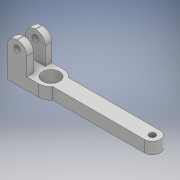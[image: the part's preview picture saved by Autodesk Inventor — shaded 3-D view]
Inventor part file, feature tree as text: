
AUTODESK INVENTOR PART (.ipt)
format: ipt  version: 2017 (Build 210142000, 142)  size: 168,960 bytes
history: native  units: mm
features: extrude x5, sketch x5, fillet x1
ambient origin geometry x8: Origin, YZ Plane, XZ Plane, XY Plane, X Axis, Y Axis, Z Axis, Center Point
bodies: Solid1 (feature_tree)
feature tree (11):
  extrude  "Extrusion1"  Depth=5.0mm
  extrude  "Extrusion2"  Depth=15.0mm TaperAngle=0.0deg
  extrude  "Extrusion3"  Depth=15.0mm
  fillet  "Fillet1"  Radius=35.0mm
  extrude  "Extrusion4"  Depth=10.0mm
  extrude  "Extrusion5"  Depth=12.0mm
  sketch  "Sketch1"  dims[d0=22.0mm d1=5.0mm]
  sketch  "Sketch2"  dims[d2=40.0mm d3=15.0mm d4=0.0mm]
  sketch  "Sketch3"  dims[d5=25.0mm d6=15.0mm d7=35.0mm d8=0.0mm]
  sketch  "Sketch4"  dims[d9=8.0mm d10=10.0mm]
  sketch  "Sketch5"  dims[d11=25.0mm d12=0.0mm d13=12.0mm d14=16.0mm d15=1.0mm d16=0.0mm d17=100.0mm d18=130.0mm d19=7.895822mm d20=10.0mm d21=8.0mm d22=3.0mm d23=0.0mm]
